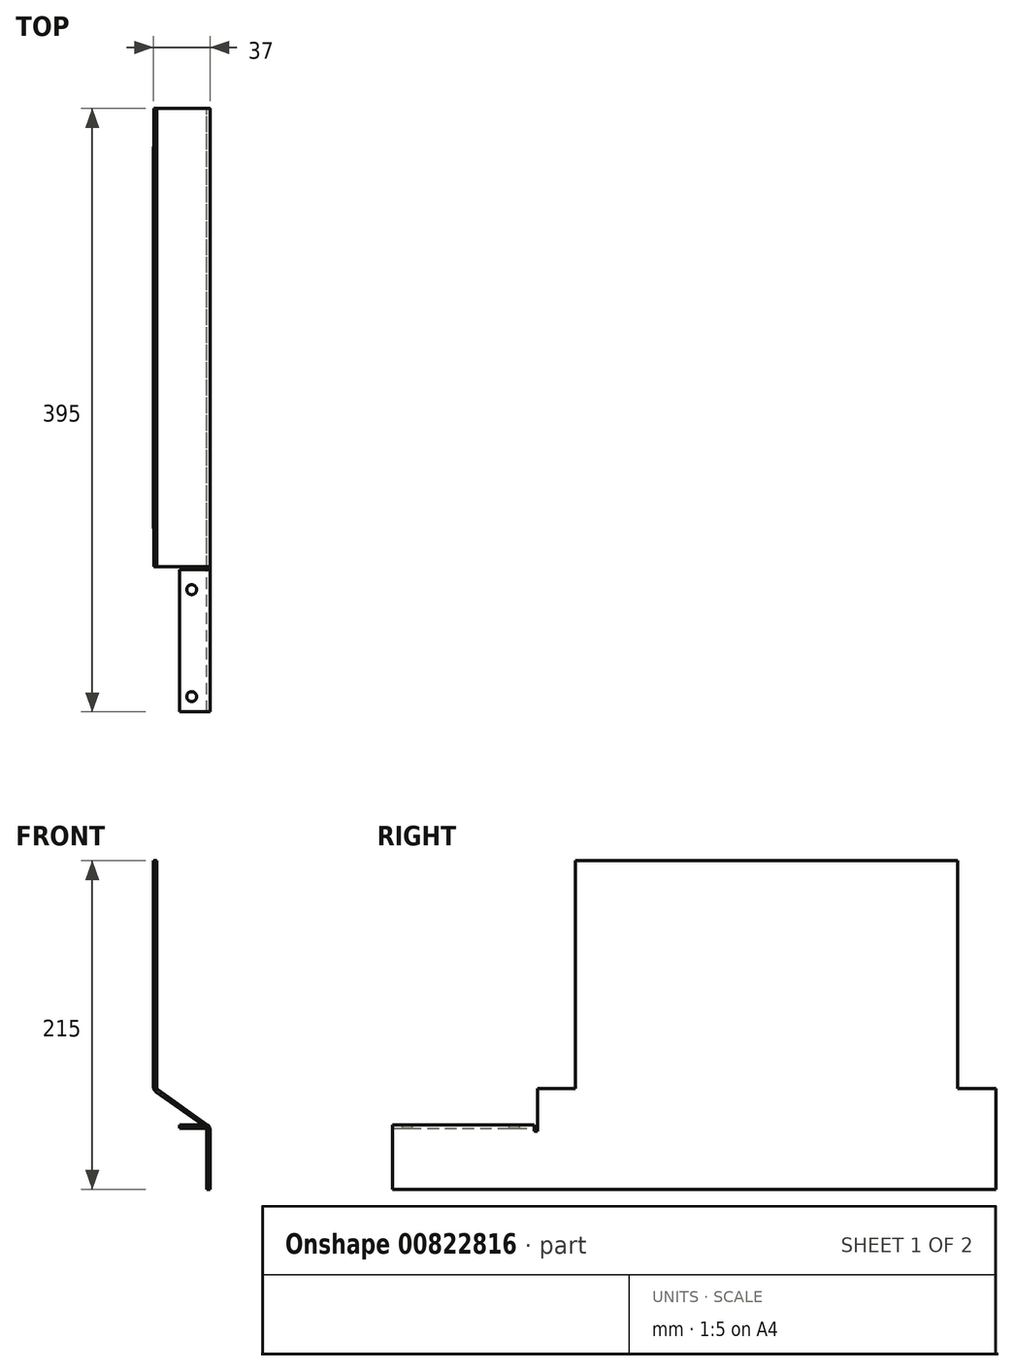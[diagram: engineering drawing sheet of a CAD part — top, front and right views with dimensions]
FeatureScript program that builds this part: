
annotation { "Feature Type Name" : "Feature", "Feature Type Description" : "" }
export const myFeature = defineFeature(function(context is Context, id is Id, definition is map)
    precondition{}
    {
        {
            var Q0;
            Q0=qCreatedBy(makeId("Front.planeOp"),FACE);
            var sketch = newSketch(context, id + "F0", { "sketchPlane" : qUnion([Q0])});
            skLineSegment(sketch, "E0", {"start": v(-66.32, 0) * mm, "end": v(0, 0) * mm, "construction": true});
            skLineSegment(sketch, "E1", {"start": v(0, 0) * mm, "end": v(0, -24) * mm, "construction": true});
            skLineSegment(sketch, "E2", {"start": v(0, -24) * mm, "end": v(0, -36) * mm, "construction": true});
            skLineSegment(sketch, "E3", {"start": v(0, -36) * mm, "end": v(0, -70) * mm, "construction": true});
            skLineSegment(sketch, "E4", {"start": v(0, -36) * mm, "end": v(-40, -36) * mm, "construction": true});
            skLineSegment(sketch, "E5", {"start": v(-40, -36) * mm, "end": v(-42.5, -36) * mm, "construction": true});
            skLineSegment(sketch, "E6", {"start": v(-42.5, -36) * mm, "end": v(-42.5, -24) * mm, "construction": true});
            skLineSegment(sketch, "E7", {"start": v(-42.5, -24) * mm, "end": v(-52.5, -24) * mm, "construction": true});
            skLineSegment(sketch, "E8", {"start": v(-52.5, -24) * mm, "end": v(-52.5, 0) * mm, "construction": true});
            skLineSegment(sketch, "E9", {"start": v(-42.5, 0) * mm, "end": v(-42.5, 150) * mm, "construction": true});
            skLineSegment(sketch, "E10", {"start": v(0, -70) * mm, "end": v(5, -70) * mm, "construction": true});
            skLineSegment(sketch, "E11", {"start": v(5, -70) * mm, "end": v(5, 55) * mm, "construction": true});
            skLineSegment(sketch, "E12", {"start": v(1, -66) * mm, "end": v(1, -26) * mm});
            skLineSegment(sketch, "E13", {"start": v(1, -26) * mm, "end": v(-34, -1) * mm});
            skLineSegment(sketch, "E14", {"start": v(-34, -1) * mm, "end": v(-34, 149) * mm});
            skLineSegment(sketch, "E15.0", {"start": v(-32, 0.03) * mm, "end": v(-32, 149) * mm});
            skLineSegment(sketch, "E15.1", {"start": v(3, -24.97) * mm, "end": v(-32, 0.03) * mm});
            skLineSegment(sketch, "E15.2", {"start": v(3, -66) * mm, "end": v(3, -24.97) * mm});
            skLineSegment(sketch, "E16", {"start": v(-34, 149) * mm, "end": v(-32, 149) * mm});
            skLineSegment(sketch, "E17", {"start": v(1, -66) * mm, "end": v(3, -66) * mm});
            skSolve(sketch);
        }
        {
            var Q0;
            Q0 = qSketchRegion(id + "F0", true);
            extrude(context, id + "F1", {"entities" : qUnion([Q0]), "endBound" : BoundingType.SYMMETRIC, "depth" : 300 * mm, "offsetDistance" : 25 * mm});
        }
        {
            var Q0;
            Q0=makeQuery(id+"F1.opExtrude","CAP_FACE",FACE,{"disambiguationData":[OSD([sQuery(id+"F0.wireOp",EDGE,"E12"),sQuery(id+"F0.wireOp",EDGE,"E13"),sQuery(id+"F0.wireOp",EDGE,"E14"),sQuery(id+"F0.wireOp",EDGE,"E15.0"),sQuery(id+"F0.wireOp",EDGE,"E15.1"),sQuery(id+"F0.wireOp",EDGE,"E15.2"),sQuery(id+"F0.wireOp",EDGE,"E16"),sQuery(id+"F0.wireOp",EDGE,"E17")])],"isStart":false});
            var sketch = newSketch(context, id + "F2", { "sketchPlane" : qUnion([Q0])});
            skLineSegment(sketch, "E18.0", {"start": v(1, -66) * mm, "end": v(1, -27.03) * mm});
            skLineSegment(sketch, "E19.0", {"start": v(3, -66) * mm, "end": v(3, -24.97) * mm});
            skLineSegment(sketch, "E20.0", {"start": v(-66.32, 0) * mm, "end": v(0, 0) * mm, "construction": true});
            skPoint(sketch, "E21.0", {"position": v(-47.5, -24) * mm});
            skLineSegment(sketch, "E22.0", {"start": v(-42.5, -24) * mm, "end": v(-52.5, -24) * mm, "construction": true});
            skLineSegment(sketch, "E23", {"start": v(-42.5, -24) * mm, "end": v(16.52, -24) * mm, "construction": true});
            skLineSegment(sketch, "E24", {"start": v(3, -24) * mm, "end": v(-17, -24) * mm});
            skLineSegment(sketch, "E25", {"start": v(-17, -24) * mm, "end": v(-17, -26) * mm});
            skLineSegment(sketch, "E26", {"start": v(-17, -26) * mm, "end": v(1, -26) * mm});
            skLineSegment(sketch, "E27", {"start": v(1, -27.03) * mm, "end": v(1, -26) * mm});
            skLineSegment(sketch, "E28", {"start": v(3, -24.97) * mm, "end": v(3, -24) * mm});
            skSolve(sketch);
        }
        {
            var Q0;
            {var subQ5=sQuery(id+"F2.wireOp",EDGE,"E28");Q0=makeQuery(id+"F2.imprint","IMPRINT",FACE,{"disambiguationData":[TD([[makeQuery(id+"F2.imprint","IMPRINT",EDGE,{"derivedFrom":subQ5}),1.0]])]});}
            var Q1;
            {var subQ7=sQuery(id+"F2.wireOp",EDGE,"E25");Q1=makeQuery(id+"F2.imprint","IMPRINT",FACE,{"disambiguationData":[TD([[makeQuery(id+"F2.imprint","IMPRINT",EDGE,{"derivedFrom":subQ7}),1.0]])]});}
            var Q2;
            Q2=makeQuery(id+"F2.imprint","IMPRINT",FACE,{"disambiguationData":[TD([[makeQuery(id+"F2.imprint","IMPRINT",EDGE,{"derivedFrom":sQuery(id+"F2.wireOp",EDGE,"E18.0")}),-1.0]])]});
            extrude(context, id + "F3", {"entities" : qUnion([Q0, Q1, Q2]), "operationType" : NewBodyOperationType.ADD, "depth" : 95 * mm, "offsetDistance" : 25 * mm});
        }
        {
            var Q0;
            {var subQ0=sQuery(id+"F2.wireOp",EDGE,"E28");var subQ1=sQuery(id+"F2.wireOp",EDGE,"E19.0");Q0=makeQuery(id+"F2KFvbb7QatC9ZH_1.1.F3.boolean.opBoolean","MERGE",FACE,{"derivedFrom":[makeQuery(id+"F3.boolean.opBoolean","MERGE",FACE,{"derivedFrom":[makeQuery(id+"F1.opExtrude","SWEPT_FACE",FACE,{"disambiguationData":[OSD([sQuery(id+"F0.wireOp",EDGE,"E15.2")])]}),makeQuery(id+"F3.opExtrude","SWEPT_FACE",FACE,{"disambiguationData":[OSD([subQ1,subQ0])]})]}),makeQuery(id+"F2KFvbb7QatC9ZH_1.1.F3.opExtrude","SWEPT_FACE",FACE,{"disambiguationData":[OSD([subQ1,subQ0])]})]});}
            var sketch = newSketch(context, id + "F4", { "sketchPlane" : qUnion([Q0])});
            skLineSegment(sketch, "E29", {"start": v(0, 168.86) * mm, "end": v(0, 0) * mm, "construction": true});
            skLineSegment(sketch, "E30", {"start": v(0, 0) * mm, "end": v(-151, 0) * mm, "construction": true});
            skLineSegment(sketch, "E31.bottom", {"start": v(-150, -28) * mm, "end": v(-152, -28) * mm});
            skLineSegment(sketch, "E31.top", {"start": v(-150, 28) * mm, "end": v(-152, 28) * mm});
            skLineSegment(sketch, "E31.left", {"start": v(-150, -28) * mm, "end": v(-150, 28) * mm});
            skLineSegment(sketch, "E31.right", {"start": v(-152, -28) * mm, "end": v(-152, 28) * mm});
            skPoint(sketch, "E31.middle", {"position": v(-151, 0) * mm});
            skLineSegment(sketch, "E32.0", {"start": v(-150, 1.06) * mm, "end": v(-150, 149) * mm, "construction": true});
            skLineSegment(sketch, "E33.0", {"start": v(-245, -24) * mm, "end": v(-150, -24) * mm, "construction": true});
            skLineSegment(sketch, "E34.MirrorCS", {"start": v(150, 28) * mm, "end": v(152, 28) * mm});
            skLineSegment(sketch, "E35.MirrorCS", {"start": v(150, -28) * mm, "end": v(152, -28) * mm});
            skPoint(sketch, "E36.MirrorP", {"position": v(151, 0) * mm});
            skLineSegment(sketch, "E37.MirrorCS", {"start": v(150, -28) * mm, "end": v(150, 28) * mm});
            skLineSegment(sketch, "E38.MirrorCS", {"start": v(152, -28) * mm, "end": v(152, 28) * mm});
            skSolve(sketch);
        }
        {
            var Q0;
            {var subQ12=sQuery(id+"F4.wireOp",EDGE,"E31.bottom");Q0=makeQuery(id+"F4.imprint","IMPRINT",FACE,{"disambiguationData":[TD([[makeQuery(id+"F4.imprint","IMPRINT",EDGE,{"derivedFrom":subQ12}),1.0]])]});}
            var sketch = newSketch(context, id + "F5", { "sketchPlane" : qUnion([Q0])});
            skLineSegment(sketch, "E39", {"start": v(-186.5, 0) * mm, "end": v(180.45, 0) * mm, "construction": true});
            skLineSegment(sketch, "E40", {"start": v(180.45, 0) * mm, "end": v(180.45, 188.38) * mm});
            skLineSegment(sketch, "E41", {"start": v(180.45, 188.38) * mm, "end": v(125, 188.38) * mm});
            skLineSegment(sketch, "E42", {"start": v(125, 188.38) * mm, "end": v(125, 0) * mm});
            skLineSegment(sketch, "E43", {"start": v(125, 0) * mm, "end": v(180.45, 0) * mm});
            skLineSegment(sketch, "E44", {"start": v(0, 0) * mm, "end": v(0, 248.71) * mm, "construction": true});
            skLineSegment(sketch, "E45.MirrorCS", {"start": v(-180.45, 0) * mm, "end": v(-180.45, 188.38) * mm});
            skLineSegment(sketch, "E46.MirrorCS", {"start": v(-180.45, 188.38) * mm, "end": v(-125, 188.38) * mm});
            skLineSegment(sketch, "E47.MirrorCS", {"start": v(-125, 0) * mm, "end": v(-180.45, 0) * mm});
            skLineSegment(sketch, "E48.MirrorCS", {"start": v(-125, 188.38) * mm, "end": v(-125, 0) * mm});
            skSolve(sketch);
        }
        {
            var Q0;
            Q0 = qSketchRegion(id + "F4", true);
            extrude(context, id + "F6", {"entities" : qUnion([Q0]), "operationType" : NewBodyOperationType.REMOVE, "oppositeDirection" : true, "depth" : 25 * mm, "offsetDistance" : 25 * mm});
        }
        {
            var Q0;
            Q0 = qSketchRegion(id + "F5", true);
            extrude(context, id + "F7", {"entities" : qUnion([Q0]), "operationType" : NewBodyOperationType.REMOVE, "oppositeDirection" : true, "depth" : 50 * mm, "offsetDistance" : 25 * mm});
        }
        {
            var Q0;
            Q0=makeQuery(id+"F1.opExtrude","SWEPT_EDGE",EDGE,{"disambiguationData":[OSD([sQuery(id+"F0.wireOp",EDGE,"E15.0"),sQuery(id+"F0.wireOp",EDGE,"E15.1")])]});
            var Q1;
            Q1=makeQuery(id+"F3.opExtrude","SWEPT_EDGE",EDGE,{"disambiguationData":[OSD([sQuery(id+"F0.wireOp",EDGE,"E13"),sQuery(id+"F2.wireOp",EDGE,"E26"),sQuery(id+"F2.wireOp",EDGE,"E27")])]});
            var Q2;
            Q2=makeQuery(id+"F1.opExtrude","SWEPT_EDGE",EDGE,{"disambiguationData":[OSD([sQuery(id+"F0.wireOp",EDGE,"E12"),sQuery(id+"F0.wireOp",EDGE,"E13")])]});
            var Q3;
            Q3=makeQuery(id+"F2KFvbb7QatC9ZH_1.1.F3.opExtrude","SWEPT_EDGE",EDGE,{"disambiguationData":[OSD([sQuery(id+"F0.wireOp",EDGE,"E13"),sQuery(id+"F2.wireOp",EDGE,"E26"),sQuery(id+"F2.wireOp",EDGE,"E27")])]});
            fillet(context, id + "F8", {"entities" : qUnion([Q0, Q1, Q2, Q3]), "radius" : 2 * mm, "tangentPropagation" : true, "allowEdgeOverflow" : false});
        }
        {
            var Q0;
            Q0=makeQuery(id+"F3.opExtrude","SWEPT_EDGE",EDGE,{"disambiguationData":[OSD([sQuery(id+"F2.wireOp",EDGE,"E24"),sQuery(id+"F2.wireOp",EDGE,"E28")])]});
            var Q1;
            Q1=makeQuery(id+"F1.opExtrude","SWEPT_EDGE",EDGE,{"disambiguationData":[OSD([sQuery(id+"F0.wireOp",EDGE,"E15.1"),sQuery(id+"F0.wireOp",EDGE,"E15.2")])]});
            var Q2;
            Q2=makeQuery(id+"F2KFvbb7QatC9ZH_1.1.F3.opExtrude","SWEPT_EDGE",EDGE,{"disambiguationData":[OSD([sQuery(id+"F2.wireOp",EDGE,"E24"),sQuery(id+"F2.wireOp",EDGE,"E28")])]});
            var Q3;
            Q3=makeQuery(id+"F1.opExtrude","SWEPT_EDGE",EDGE,{"disambiguationData":[OSD([sQuery(id+"F0.wireOp",EDGE,"E13"),sQuery(id+"F0.wireOp",EDGE,"E14")])]});
            fillet(context, id + "F9", {"entities" : qUnion([Q0, Q1, Q2, Q3]), "radius" : 4 * mm, "tangentPropagation" : true, "allowEdgeOverflow" : false});
        }
        {
            var Q0;
            Q0=makeQuery(id+"F3.opExtrude","SWEPT_FACE",FACE,{"disambiguationData":[OSD([sQuery(id+"F2.wireOp",EDGE,"E24")])]});
            var sketch = newSketch(context, id + "F10", { "sketchPlane" : qUnion([Q0])});
            skLineSegment(sketch, "E49", {"start": v(0, 0) * mm, "end": v(-131.96, 0) * mm, "construction": true});
            skLineSegment(sketch, "E50", {"start": v(-9, 235) * mm, "end": v(-9, 165) * mm, "construction": true});
            skLineSegment(sketch, "E51.0", {"start": v(3, 245) * mm, "end": v(3, 152) * mm, "construction": true});
            skPoint(sketch, "E52", {"position": v(-9, 200) * mm});
            skCircle(sketch, "E53", {"center": v(-9, 235) * mm, "radius": 3.25 * mm});
            skCircle(sketch, "E54", {"center": v(-9, 165) * mm, "radius": 3.25 * mm});
            skCircle(sketch, "E55.MirrorC", {"center": v(-9, -165) * mm, "radius": 3.25 * mm});
            skCircle(sketch, "E56.MirrorC", {"center": v(-9, -235) * mm, "radius": 3.25 * mm});
            skSolve(sketch);
        }
        {
            var Q0;
            Q0 = qSketchRegion(id + "F10", true);
            extrude(context, id + "F11", {"entities" : qUnion([Q0]), "operationType" : NewBodyOperationType.REMOVE, "oppositeDirection" : true, "depth" : 25 * mm, "offsetDistance" : 25 * mm});
        }
    });
